# Revit family: Shower-Rainhead_Kit-KALLISTA-For_Town-P21540-1
name_source: partatom
category: Plumbing Fixtures
units: mm (PartAtom-declared; Revit-internal decimal feet)

## family parameters
Cut with Voids When Loaded = No
Host = Face
Maintain Annotation Orientation = No
OmniClass Number = 23.31.17.00
Part Type = Normal
Room Calculation Point = No
Round Connector Dimension = Use Diameter
Shared = No

## types (5) — shared parameters
ADA Compliant = No
Assembly Code = D2010700
CW Connection = No
Cold Water Inlet = Cold Water Inlet
Date Modified = 05/04/2025
Default Elevation = 0"
Drain Included = No
HW Connection = Yes
Hot Water Inlet = Hot Water Inlet
Length = 8 3/4"
Manufacturer = Kallista Co.
Master Format 2014 = 22 42 23
Master Format 2014 Name = Residential Showers
Material = Premium Metal Construction
Pressure = 80.00 psi
Product Documentation Link = https://techcomm.kohler.com
Product Name = For Town
Product Page URL = https://www.kallista.com
Tempered Water Inlet = Tempered Water Inlet
URL = https://www.kallista.com
Vent Connection = No
Waste Connection = No
Waste Water Outlet = Waste Water Outlet
WaterSense Certified = No
Width = 8 3/4"

## per-type parameters (varying)
| type | Description | Finish | Flow Rate | Model | Type |
| 1.75 GPM, AD-Nickel Silver | Air-Induction ECO Rain Showerhead | Kallista-Metal-AD-Nickel_Silver | 2 GPM | P21540-G-AD | 5 |
| 2.5 GPM, CP-Chrome | Air-Induction Rain Showerhead | Kallista-Metal-CP-Chrome | 3 GPM | P21540-00-CP | 2 |
| 2.5 GPM, YG-Matte Gold | Air-Induction Rain Showerhead | Kallista-Metal-YG-Matte_Gold | 3 GPM | P21540-00-YG | 3 |
| 1.75 GPM, CP-Chrome | Air-Induction ECO Rain Showerhead | Kallista-Metal-CP-Chrome | 2 GPM | P21540-G-CP | 4 |
| 2.5 GPM, AD-Nickel Silver | Air-Induction Rain Showerhead | Kallista-Metal-AD-Nickel_Silver | 3 GPM | P21540-00-AD | 1 |

## geometry (parser evidence)
native form markers: Sweep x8
no freeform markers — native parametric forms only
